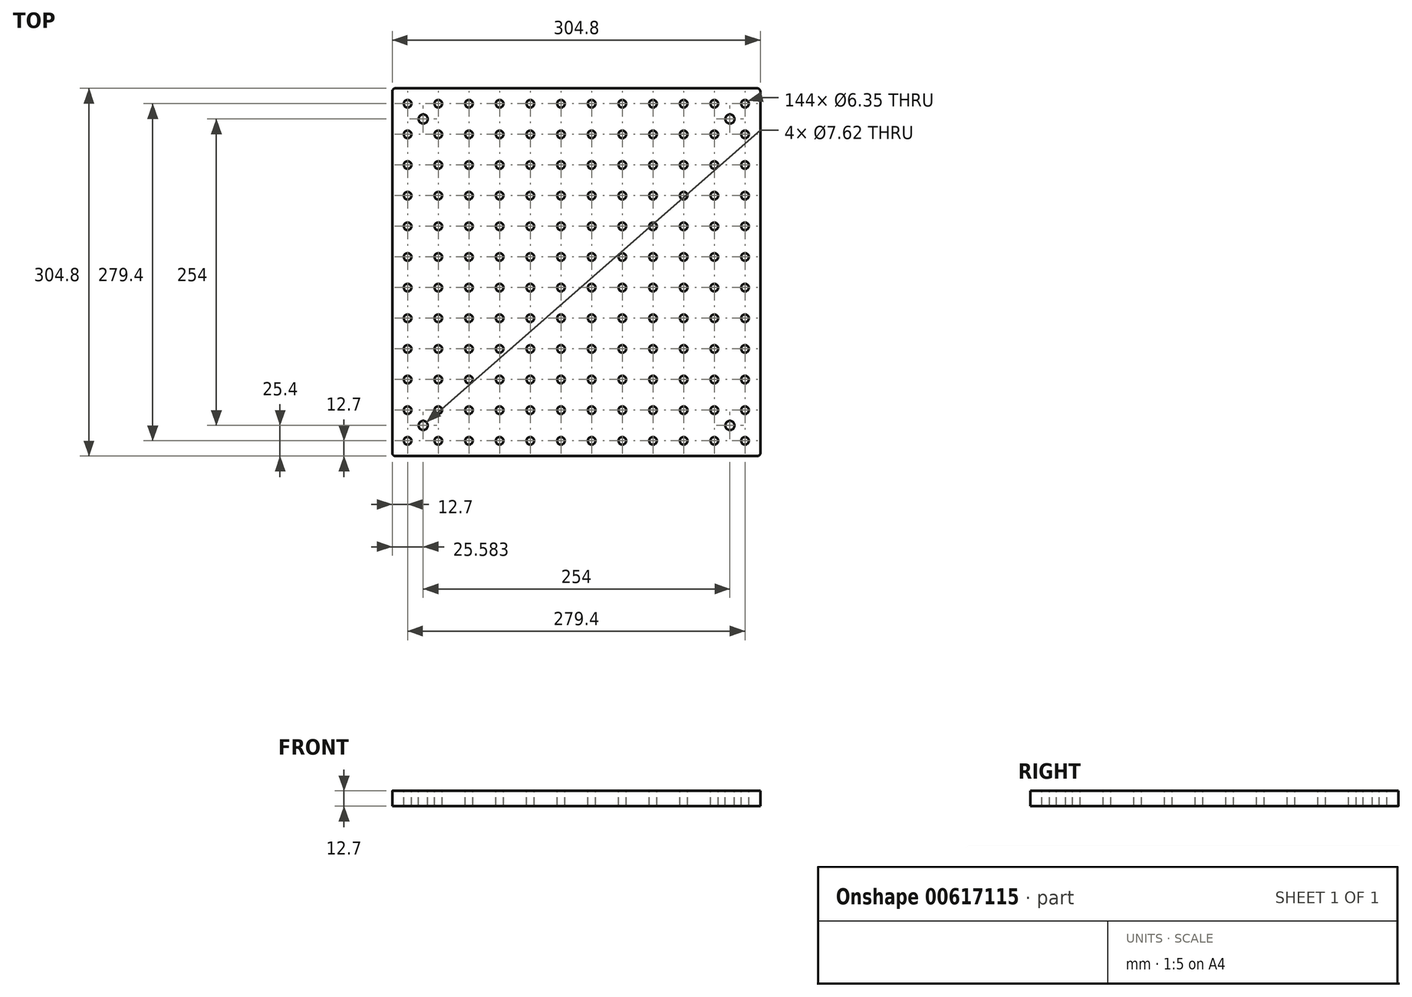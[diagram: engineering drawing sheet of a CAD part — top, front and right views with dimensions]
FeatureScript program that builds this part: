
annotation { "Feature Type Name" : "Feature", "Feature Type Description" : "" }
export const myFeature = defineFeature(function(context is Context, id is Id, definition is map)
    precondition{}
    {
        {
            var Q0;
            Q0=qCreatedBy(makeId("Top.planeOp"),FACE);
            var sketch = newSketch(context, id + "F0", { "sketchPlane" : qUnion([Q0])});
            skLineSegment(sketch, "E0.bottom", {"start": v(-152.4, 152.4) * mm, "end": v(152.4, 152.4) * mm});
            skLineSegment(sketch, "E0.top", {"start": v(-152.4, -152.4) * mm, "end": v(152.4, -152.4) * mm});
            skLineSegment(sketch, "E0.left", {"start": v(-152.4, 152.4) * mm, "end": v(-152.4, -152.4) * mm});
            skLineSegment(sketch, "E0.right", {"start": v(152.4, 152.4) * mm, "end": v(152.4, -152.4) * mm});
            skSolve(sketch);
        }
        {
            var Q0;
            Q0 = qSketchRegion(id + "F0", true);
            extrude(context, id + "F1", {"entities" : qUnion([Q0]), "depth" : 12.7 * mm, "offsetDistance" : 25.4 * mm});
        }
        {
            var Q0;
            Q0=makeQuery(id+"F1.opExtrude","CAP_FACE",FACE,{"disambiguationData":[OSD([sQuery(id+"F0.wireOp",EDGE,"E0.bottom"),sQuery(id+"F0.wireOp",EDGE,"E0.top"),sQuery(id+"F0.wireOp",EDGE,"E0.left"),sQuery(id+"F0.wireOp",EDGE,"E0.right")])],"isStart":false});
            var sketch = newSketch(context, id + "F2", { "sketchPlane" : qUnion([Q0])});
            skCircle(sketch, "E1", {"center": v(-139.7, -139.7) * mm, "radius": 3.18 * mm});
            skCircle(sketch, "E2.0.1.0", {"center": v(-139.7, -114.3) * mm, "radius": 3.18 * mm});
            skCircle(sketch, "E2.0.2.0", {"center": v(-139.7, -88.9) * mm, "radius": 3.18 * mm});
            skCircle(sketch, "E2.0.3.0", {"center": v(-139.7, -63.5) * mm, "radius": 3.18 * mm});
            skCircle(sketch, "E2.0.4.0", {"center": v(-139.7, -38.1) * mm, "radius": 3.18 * mm});
            skCircle(sketch, "E2.0.5.0", {"center": v(-139.7, -12.7) * mm, "radius": 3.18 * mm});
            skCircle(sketch, "E2.0.6.0", {"center": v(-139.7, 12.7) * mm, "radius": 3.18 * mm});
            skCircle(sketch, "E2.0.7.0", {"center": v(-139.7, 38.1) * mm, "radius": 3.18 * mm});
            skCircle(sketch, "E2.0.8.0", {"center": v(-139.7, 63.5) * mm, "radius": 3.18 * mm});
            skCircle(sketch, "E2.0.9.0", {"center": v(-139.7, 88.9) * mm, "radius": 3.18 * mm});
            skCircle(sketch, "E2.0.10.0", {"center": v(-139.7, 114.3) * mm, "radius": 3.18 * mm});
            skCircle(sketch, "E2.1.0.0", {"center": v(-114.3, -139.7) * mm, "radius": 3.18 * mm});
            skCircle(sketch, "E2.1.1.0", {"center": v(-114.3, -114.3) * mm, "radius": 3.18 * mm});
            skCircle(sketch, "E2.1.2.0", {"center": v(-114.3, -88.9) * mm, "radius": 3.18 * mm});
            skCircle(sketch, "E2.1.3.0", {"center": v(-114.3, -63.5) * mm, "radius": 3.18 * mm});
            skCircle(sketch, "E2.1.4.0", {"center": v(-114.3, -38.1) * mm, "radius": 3.18 * mm});
            skCircle(sketch, "E2.1.5.0", {"center": v(-114.3, -12.7) * mm, "radius": 3.18 * mm});
            skCircle(sketch, "E2.1.6.0", {"center": v(-114.3, 12.7) * mm, "radius": 3.18 * mm});
            skCircle(sketch, "E2.1.7.0", {"center": v(-114.3, 38.1) * mm, "radius": 3.18 * mm});
            skCircle(sketch, "E2.1.8.0", {"center": v(-114.3, 63.5) * mm, "radius": 3.18 * mm});
            skCircle(sketch, "E2.1.9.0", {"center": v(-114.3, 88.9) * mm, "radius": 3.18 * mm});
            skCircle(sketch, "E2.1.10.0", {"center": v(-114.3, 114.3) * mm, "radius": 3.18 * mm});
            skCircle(sketch, "E2.2.0.0", {"center": v(-88.9, -139.7) * mm, "radius": 3.18 * mm});
            skCircle(sketch, "E2.2.1.0", {"center": v(-88.9, -114.3) * mm, "radius": 3.18 * mm});
            skCircle(sketch, "E2.2.2.0", {"center": v(-88.9, -88.9) * mm, "radius": 3.18 * mm});
            skCircle(sketch, "E2.2.3.0", {"center": v(-88.9, -63.5) * mm, "radius": 3.18 * mm});
            skCircle(sketch, "E2.2.4.0", {"center": v(-88.9, -38.1) * mm, "radius": 3.18 * mm});
            skCircle(sketch, "E2.2.5.0", {"center": v(-88.9, -12.7) * mm, "radius": 3.18 * mm});
            skCircle(sketch, "E2.2.6.0", {"center": v(-88.9, 12.7) * mm, "radius": 3.18 * mm});
            skCircle(sketch, "E2.2.7.0", {"center": v(-88.9, 38.1) * mm, "radius": 3.18 * mm});
            skCircle(sketch, "E2.2.8.0", {"center": v(-88.9, 63.5) * mm, "radius": 3.18 * mm});
            skCircle(sketch, "E2.2.9.0", {"center": v(-88.9, 88.9) * mm, "radius": 3.18 * mm});
            skCircle(sketch, "E2.2.10.0", {"center": v(-88.9, 114.3) * mm, "radius": 3.18 * mm});
            skCircle(sketch, "E2.3.0.0", {"center": v(-63.5, -139.7) * mm, "radius": 3.18 * mm});
            skCircle(sketch, "E2.3.1.0", {"center": v(-63.5, -114.3) * mm, "radius": 3.18 * mm});
            skCircle(sketch, "E2.3.2.0", {"center": v(-63.5, -88.9) * mm, "radius": 3.18 * mm});
            skCircle(sketch, "E2.3.3.0", {"center": v(-63.5, -63.5) * mm, "radius": 3.18 * mm});
            skCircle(sketch, "E2.3.4.0", {"center": v(-63.5, -38.1) * mm, "radius": 3.18 * mm});
            skCircle(sketch, "E2.3.5.0", {"center": v(-63.5, -12.7) * mm, "radius": 3.18 * mm});
            skCircle(sketch, "E2.3.6.0", {"center": v(-63.5, 12.7) * mm, "radius": 3.18 * mm});
            skCircle(sketch, "E2.3.7.0", {"center": v(-63.5, 38.1) * mm, "radius": 3.18 * mm});
            skCircle(sketch, "E2.3.8.0", {"center": v(-63.5, 63.5) * mm, "radius": 3.18 * mm});
            skCircle(sketch, "E2.3.9.0", {"center": v(-63.5, 88.9) * mm, "radius": 3.18 * mm});
            skCircle(sketch, "E2.3.10.0", {"center": v(-63.5, 114.3) * mm, "radius": 3.18 * mm});
            skCircle(sketch, "E2.4.0.0", {"center": v(-38.1, -139.7) * mm, "radius": 3.18 * mm});
            skCircle(sketch, "E2.4.1.0", {"center": v(-38.1, -114.3) * mm, "radius": 3.18 * mm});
            skCircle(sketch, "E2.4.2.0", {"center": v(-38.1, -88.9) * mm, "radius": 3.18 * mm});
            skCircle(sketch, "E2.4.3.0", {"center": v(-38.1, -63.5) * mm, "radius": 3.18 * mm});
            skCircle(sketch, "E2.4.4.0", {"center": v(-38.1, -38.1) * mm, "radius": 3.18 * mm});
            skCircle(sketch, "E2.4.5.0", {"center": v(-38.1, -12.7) * mm, "radius": 3.18 * mm});
            skCircle(sketch, "E2.4.6.0", {"center": v(-38.1, 12.7) * mm, "radius": 3.18 * mm});
            skCircle(sketch, "E2.4.7.0", {"center": v(-38.1, 38.1) * mm, "radius": 3.18 * mm});
            skCircle(sketch, "E2.4.8.0", {"center": v(-38.1, 63.5) * mm, "radius": 3.18 * mm});
            skCircle(sketch, "E2.4.9.0", {"center": v(-38.1, 88.9) * mm, "radius": 3.18 * mm});
            skCircle(sketch, "E2.4.10.0", {"center": v(-38.1, 114.3) * mm, "radius": 3.18 * mm});
            skCircle(sketch, "E2.5.0.0", {"center": v(-12.7, -139.7) * mm, "radius": 3.18 * mm});
            skCircle(sketch, "E2.5.1.0", {"center": v(-12.7, -114.3) * mm, "radius": 3.18 * mm});
            skCircle(sketch, "E2.5.2.0", {"center": v(-12.7, -88.9) * mm, "radius": 3.18 * mm});
            skCircle(sketch, "E2.5.3.0", {"center": v(-12.7, -63.5) * mm, "radius": 3.18 * mm});
            skCircle(sketch, "E2.5.4.0", {"center": v(-12.7, -38.1) * mm, "radius": 3.18 * mm});
            skCircle(sketch, "E2.5.5.0", {"center": v(-12.7, -12.7) * mm, "radius": 3.18 * mm});
            skCircle(sketch, "E2.5.6.0", {"center": v(-12.7, 12.7) * mm, "radius": 3.18 * mm});
            skCircle(sketch, "E2.5.7.0", {"center": v(-12.7, 38.1) * mm, "radius": 3.18 * mm});
            skCircle(sketch, "E2.5.8.0", {"center": v(-12.7, 63.5) * mm, "radius": 3.18 * mm});
            skCircle(sketch, "E2.5.9.0", {"center": v(-12.7, 88.9) * mm, "radius": 3.18 * mm});
            skCircle(sketch, "E2.5.10.0", {"center": v(-12.7, 114.3) * mm, "radius": 3.18 * mm});
            skCircle(sketch, "E2.6.0.0", {"center": v(12.7, -139.7) * mm, "radius": 3.18 * mm});
            skCircle(sketch, "E2.6.1.0", {"center": v(12.7, -114.3) * mm, "radius": 3.18 * mm});
            skCircle(sketch, "E2.6.2.0", {"center": v(12.7, -88.9) * mm, "radius": 3.18 * mm});
            skCircle(sketch, "E2.6.3.0", {"center": v(12.7, -63.5) * mm, "radius": 3.18 * mm});
            skCircle(sketch, "E2.6.4.0", {"center": v(12.7, -38.1) * mm, "radius": 3.18 * mm});
            skCircle(sketch, "E2.6.5.0", {"center": v(12.7, -12.7) * mm, "radius": 3.18 * mm});
            skCircle(sketch, "E2.6.6.0", {"center": v(12.7, 12.7) * mm, "radius": 3.18 * mm});
            skCircle(sketch, "E2.6.7.0", {"center": v(12.7, 38.1) * mm, "radius": 3.18 * mm});
            skCircle(sketch, "E2.6.8.0", {"center": v(12.7, 63.5) * mm, "radius": 3.18 * mm});
            skCircle(sketch, "E2.6.9.0", {"center": v(12.7, 88.9) * mm, "radius": 3.18 * mm});
            skCircle(sketch, "E2.6.10.0", {"center": v(12.7, 114.3) * mm, "radius": 3.18 * mm});
            skCircle(sketch, "E2.7.0.0", {"center": v(38.1, -139.7) * mm, "radius": 3.18 * mm});
            skCircle(sketch, "E2.7.1.0", {"center": v(38.1, -114.3) * mm, "radius": 3.18 * mm});
            skCircle(sketch, "E2.7.2.0", {"center": v(38.1, -88.9) * mm, "radius": 3.18 * mm});
            skCircle(sketch, "E2.7.3.0", {"center": v(38.1, -63.5) * mm, "radius": 3.18 * mm});
            skCircle(sketch, "E2.7.4.0", {"center": v(38.1, -38.1) * mm, "radius": 3.18 * mm});
            skCircle(sketch, "E2.7.5.0", {"center": v(38.1, -12.7) * mm, "radius": 3.18 * mm});
            skCircle(sketch, "E2.7.6.0", {"center": v(38.1, 12.7) * mm, "radius": 3.18 * mm});
            skCircle(sketch, "E2.7.7.0", {"center": v(38.1, 38.1) * mm, "radius": 3.18 * mm});
            skCircle(sketch, "E2.7.8.0", {"center": v(38.1, 63.5) * mm, "radius": 3.18 * mm});
            skCircle(sketch, "E2.7.9.0", {"center": v(38.1, 88.9) * mm, "radius": 3.18 * mm});
            skCircle(sketch, "E2.7.10.0", {"center": v(38.1, 114.3) * mm, "radius": 3.18 * mm});
            skCircle(sketch, "E2.8.0.0", {"center": v(63.5, -139.7) * mm, "radius": 3.18 * mm});
            skCircle(sketch, "E2.8.1.0", {"center": v(63.5, -114.3) * mm, "radius": 3.18 * mm});
            skCircle(sketch, "E2.8.2.0", {"center": v(63.5, -88.9) * mm, "radius": 3.18 * mm});
            skCircle(sketch, "E2.8.3.0", {"center": v(63.5, -63.5) * mm, "radius": 3.18 * mm});
            skCircle(sketch, "E2.8.4.0", {"center": v(63.5, -38.1) * mm, "radius": 3.18 * mm});
            skCircle(sketch, "E2.8.5.0", {"center": v(63.5, -12.7) * mm, "radius": 3.18 * mm});
            skCircle(sketch, "E2.8.6.0", {"center": v(63.5, 12.7) * mm, "radius": 3.18 * mm});
            skCircle(sketch, "E2.8.7.0", {"center": v(63.5, 38.1) * mm, "radius": 3.18 * mm});
            skCircle(sketch, "E2.8.8.0", {"center": v(63.5, 63.5) * mm, "radius": 3.18 * mm});
            skCircle(sketch, "E2.8.9.0", {"center": v(63.5, 88.9) * mm, "radius": 3.18 * mm});
            skCircle(sketch, "E2.8.10.0", {"center": v(63.5, 114.3) * mm, "radius": 3.18 * mm});
            skCircle(sketch, "E2.9.0.0", {"center": v(88.9, -139.7) * mm, "radius": 3.18 * mm});
            skCircle(sketch, "E2.9.1.0", {"center": v(88.9, -114.3) * mm, "radius": 3.18 * mm});
            skCircle(sketch, "E2.9.2.0", {"center": v(88.9, -88.9) * mm, "radius": 3.18 * mm});
            skCircle(sketch, "E2.9.3.0", {"center": v(88.9, -63.5) * mm, "radius": 3.18 * mm});
            skCircle(sketch, "E2.9.4.0", {"center": v(88.9, -38.1) * mm, "radius": 3.18 * mm});
            skCircle(sketch, "E2.9.5.0", {"center": v(88.9, -12.7) * mm, "radius": 3.18 * mm});
            skCircle(sketch, "E2.9.6.0", {"center": v(88.9, 12.7) * mm, "radius": 3.18 * mm});
            skCircle(sketch, "E2.9.7.0", {"center": v(88.9, 38.1) * mm, "radius": 3.18 * mm});
            skCircle(sketch, "E2.9.8.0", {"center": v(88.9, 63.5) * mm, "radius": 3.18 * mm});
            skCircle(sketch, "E2.9.9.0", {"center": v(88.9, 88.9) * mm, "radius": 3.18 * mm});
            skCircle(sketch, "E2.9.10.0", {"center": v(88.9, 114.3) * mm, "radius": 3.18 * mm});
            skCircle(sketch, "E2.10.0.0", {"center": v(114.3, -139.7) * mm, "radius": 3.18 * mm});
            skCircle(sketch, "E2.10.1.0", {"center": v(114.3, -114.3) * mm, "radius": 3.18 * mm});
            skCircle(sketch, "E2.10.2.0", {"center": v(114.3, -88.9) * mm, "radius": 3.18 * mm});
            skCircle(sketch, "E2.10.3.0", {"center": v(114.3, -63.5) * mm, "radius": 3.18 * mm});
            skCircle(sketch, "E2.10.4.0", {"center": v(114.3, -38.1) * mm, "radius": 3.18 * mm});
            skCircle(sketch, "E2.10.5.0", {"center": v(114.3, -12.7) * mm, "radius": 3.18 * mm});
            skCircle(sketch, "E2.10.6.0", {"center": v(114.3, 12.7) * mm, "radius": 3.18 * mm});
            skCircle(sketch, "E2.10.7.0", {"center": v(114.3, 38.1) * mm, "radius": 3.18 * mm});
            skCircle(sketch, "E2.10.8.0", {"center": v(114.3, 63.5) * mm, "radius": 3.18 * mm});
            skCircle(sketch, "E2.10.9.0", {"center": v(114.3, 88.9) * mm, "radius": 3.18 * mm});
            skCircle(sketch, "E2.10.10.0", {"center": v(114.3, 114.3) * mm, "radius": 3.18 * mm});
            skLineSegment(sketch, "E2.direction1", {"start": v(-139.7, -139.7) * mm, "end": v(-114.3, -139.7) * mm, "construction": true});
            skLineSegment(sketch, "E2.direction2", {"start": v(-139.7, -139.7) * mm, "end": v(-139.7, -114.3) * mm, "construction": true});
            skCircle(sketch, "E3.0.11.0", {"center": v(139.7, -139.7) * mm, "radius": 3.18 * mm});
            skCircle(sketch, "E3.0.11.1", {"center": v(139.7, -114.3) * mm, "radius": 3.18 * mm});
            skCircle(sketch, "E3.0.11.2", {"center": v(139.7, -88.9) * mm, "radius": 3.18 * mm});
            skCircle(sketch, "E3.0.11.3", {"center": v(139.7, -63.5) * mm, "radius": 3.18 * mm});
            skCircle(sketch, "E3.0.11.4", {"center": v(139.7, -38.1) * mm, "radius": 3.18 * mm});
            skCircle(sketch, "E3.0.11.5", {"center": v(139.7, -12.7) * mm, "radius": 3.18 * mm});
            skCircle(sketch, "E3.0.11.6", {"center": v(139.7, 12.7) * mm, "radius": 3.18 * mm});
            skCircle(sketch, "E3.0.11.7", {"center": v(139.7, 38.1) * mm, "radius": 3.18 * mm});
            skCircle(sketch, "E3.0.11.8", {"center": v(139.7, 63.5) * mm, "radius": 3.18 * mm});
            skCircle(sketch, "E3.0.11.9", {"center": v(139.7, 88.9) * mm, "radius": 3.18 * mm});
            skCircle(sketch, "E3.0.11.10", {"center": v(139.7, 114.3) * mm, "radius": 3.18 * mm});
            skCircle(sketch, "E4.0.0.11", {"center": v(-139.7, 139.7) * mm, "radius": 3.18 * mm});
            skCircle(sketch, "E4.0.1.11", {"center": v(-114.3, 139.7) * mm, "radius": 3.18 * mm});
            skCircle(sketch, "E4.0.2.11", {"center": v(-88.9, 139.7) * mm, "radius": 3.18 * mm});
            skCircle(sketch, "E4.0.3.11", {"center": v(-63.5, 139.7) * mm, "radius": 3.18 * mm});
            skCircle(sketch, "E4.0.4.11", {"center": v(-38.1, 139.7) * mm, "radius": 3.18 * mm});
            skCircle(sketch, "E4.0.5.11", {"center": v(-12.7, 139.7) * mm, "radius": 3.18 * mm});
            skCircle(sketch, "E4.0.6.11", {"center": v(12.7, 139.7) * mm, "radius": 3.18 * mm});
            skCircle(sketch, "E4.0.7.11", {"center": v(38.1, 139.7) * mm, "radius": 3.18 * mm});
            skCircle(sketch, "E4.0.8.11", {"center": v(63.5, 139.7) * mm, "radius": 3.18 * mm});
            skCircle(sketch, "E4.0.9.11", {"center": v(88.9, 139.7) * mm, "radius": 3.18 * mm});
            skCircle(sketch, "E4.0.10.11", {"center": v(114.3, 139.7) * mm, "radius": 3.18 * mm});
            skCircle(sketch, "E4.0.11.11", {"center": v(139.7, 139.7) * mm, "radius": 3.18 * mm});
            skCircle(sketch, "E5", {"center": v(-126.82, -127) * mm, "radius": 3.81 * mm});
            skCircle(sketch, "E6.0.1.0", {"center": v(-126.82, 127) * mm, "radius": 3.81 * mm});
            skCircle(sketch, "E6.1.0.0", {"center": v(127.18, -127) * mm, "radius": 3.81 * mm});
            skCircle(sketch, "E6.1.1.0", {"center": v(127.18, 127) * mm, "radius": 3.81 * mm});
            skCircle(sketch, "E6.2.0.0", {"center": v(381.18, -127) * mm, "radius": 3.81 * mm});
            skCircle(sketch, "E6.2.1.0", {"center": v(381.18, 127) * mm, "radius": 3.81 * mm});
            skLineSegment(sketch, "E6.direction1", {"start": v(-126.82, -127) * mm, "end": v(127.18, -127) * mm, "construction": true});
            skLineSegment(sketch, "E6.direction2", {"start": v(-126.82, -127) * mm, "end": v(-126.82, 127) * mm, "construction": true});
            skSolve(sketch);
        }
        {
            var Q0;
            Q0 = qSketchRegion(id + "F2", true);
            extrude(context, id + "F3", {"entities" : qUnion([Q0]), "operationType" : NewBodyOperationType.REMOVE, "oppositeDirection" : true, "depth" : 25.4 * mm, "offsetDistance" : 25.4 * mm});
        }
        {
            var Q0;
            Q0=makeQuery(id+"F1.opExtrude","SWEPT_EDGE",EDGE,{"disambiguationData":[OSD([sQuery(id+"F0.wireOp",EDGE,"E0.bottom"),sQuery(id+"F0.wireOp",EDGE,"E0.left")])]});
            var Q1;
            Q1=makeQuery(id+"F1.opExtrude","SWEPT_EDGE",EDGE,{"disambiguationData":[OSD([sQuery(id+"F0.wireOp",EDGE,"E0.bottom"),sQuery(id+"F0.wireOp",EDGE,"E0.right")])]});
            var Q2;
            Q2=makeQuery(id+"F1.opExtrude","SWEPT_EDGE",EDGE,{"disambiguationData":[OSD([sQuery(id+"F0.wireOp",EDGE,"E0.top"),sQuery(id+"F0.wireOp",EDGE,"E0.left")])]});
            var Q3;
            Q3=makeQuery(id+"F1.opExtrude","SWEPT_EDGE",EDGE,{"disambiguationData":[OSD([sQuery(id+"F0.wireOp",EDGE,"E0.top"),sQuery(id+"F0.wireOp",EDGE,"E0.right")])]});
            fillet(context, id + "F4", {"entities" : qUnion([Q0, Q1, Q2, Q3]), "radius" : 2.54 * mm, "tangentPropagation" : true, "allowEdgeOverflow" : false});
        }
    });
